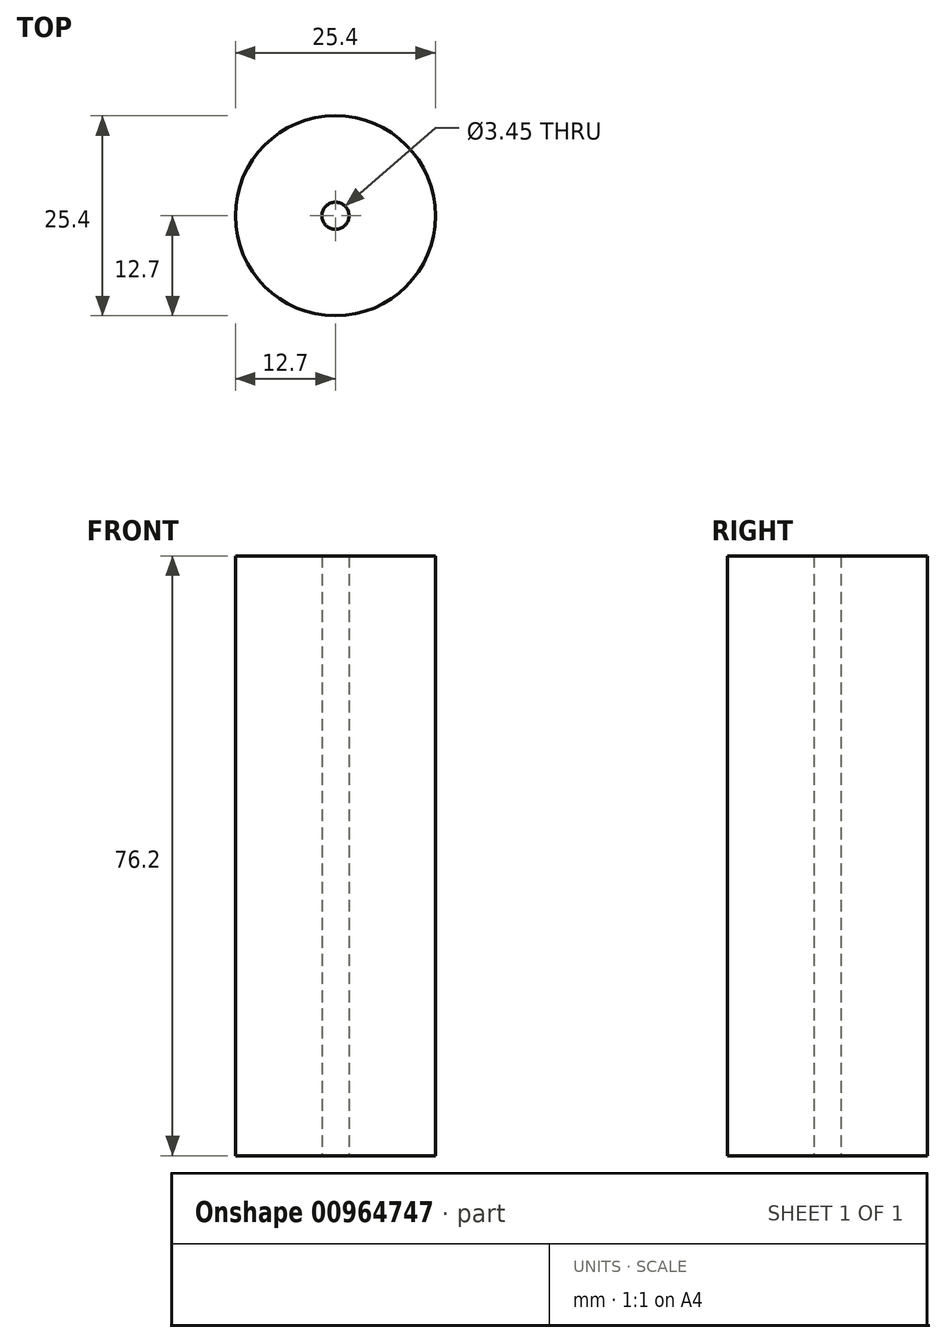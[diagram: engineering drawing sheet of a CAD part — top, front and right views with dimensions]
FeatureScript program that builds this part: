
annotation { "Feature Type Name" : "Feature", "Feature Type Description" : "" }
export const myFeature = defineFeature(function(context is Context, id is Id, definition is map)
    precondition{}
    {
        {
            var Q0;
            Q0=qCreatedBy(makeId("Top.planeOp"),FACE);
            var sketch = newSketch(context, id + "F0", { "sketchPlane" : qUnion([Q0])});
            skCircle(sketch, "E0", {"center": v(0, 0) * mm, "radius": 12.7 * mm});
            skCircle(sketch, "E1", {"center": v(0, 0) * mm, "radius": 1.73 * mm});
            skSolve(sketch);
        }
        {
            var Q0;
            Q0 = qSketchRegion(id + "F0", true);
            extrude(context, id + "F1", {"entities" : qUnion([Q0]), "depth" : 76.2 * mm, "offsetDistance" : 25.4 * mm});
        }
    });
